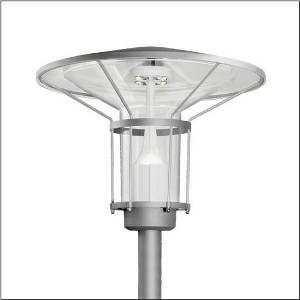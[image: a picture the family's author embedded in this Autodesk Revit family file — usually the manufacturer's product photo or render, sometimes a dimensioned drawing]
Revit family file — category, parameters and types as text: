
# Revit family: laterne_classic___st1_2a_5xa5245ef14h_27d9
name_source: partatom
category: Lighting Fixtures
units: mm (PartAtom-declared; Revit-internal decimal feet)

## family parameters
Cut with Voids When Loaded = No
Host = Face
Light Source = No
Part Type = Normal
Room Calculation Point = No
Round Connector Dimension = Use Diameter
Shared = No

## types (1)
- --- (1 x LED, 1380 lm, 10.5 W, 3000K)
    Apparent Load = 11 VA
    CIE Flux Codes = 21 60 93 97 100
    Color Rendering = 70
    Color Temperature = 3000K
    Default Elevation = 1800 mm
    Description = Lantern Classic, mast luminaire, Module 540 iQ-SR, primary light control with 3 zone facetted reflector, of plastic, silver coated, highly specular, structured, primary optical cover: cover, of PMMA, transparent, light distribution: ST1.2a, light emission: direct distribution, primary light characteristic: asymmetric, installation type: post-top, LED, High Power LED, rated luminous flux: 1.380lm, luminous efficacy: 131lm/W, light colour: 730, colour temperature: 3000K, control gear: ECG iQ, control: Auto-Match, Temp-Guard, Lumen-Switch, Night-Set, Smart-Wire, Light-Fading, Desk-Remote (wireless, voltage-free reading and setting of iQ features in the workshop via application-optimized NFC function/RFID function), optimised constant luminous flux control (CLO 2.0), Street-Remote, presetting dimming logarithmic, with terminal, 6-pole, max. 2.5mm², mains connection: 220..240V, AC, 50/60Hz, start of lifetime: 11W, end of lifetime: 11W, reduction: 5W, luminaire housing, upper part, of glass-fibre reinforced polyester, coated, Siteco® metallic grey (DB 702S), diameter: 750mm, height: 596mm, spigot size: d x l = 76 x 70mm (post-top) | with reducer (optional accessory) 60 x 70mm, post-top mast mounting element, of diecast aluminium, coated, Siteco® metallic grey (DB 702S), Module 540 iQ-SR, traffic white (RAL 9016), equipment: standard, protection rating (complete): IP65, insulation class (complete): insulation class II (safety insulation), certification: CE, ENEC, VDE, packaging unit: 1 piece

Light Distribution: ST1.2a
    Height = 596 mm
    Lamp = 1 x LED
    Lamp Light Flux = 1380 lm
    Lamp Power = 10.5 W
    Lamp count = 1
    Length = 750 mm
    Luminous efficacy = 131 lm/W
    Manufacturer = Siteco
    ModVariant = No
    Model = 5XA5245EF14H
    Number of Poles = 1
    OnlyDefault = Yes
    Power Factor = 1
    Product Name = Laterne Classic | ST1.2a
    Product group = mast luminaire | pylon top
    ProductGroupID = 6100
    Protection Class = Protection class II
    Protection Degree = IP 65
    RLX_Detail_Level = 1
    RlxData = <blob elided: 91801 chars, md5=6b808954>
    Socket = socket
    Standby Power = 0 W
    System Light Flux = 1380 lm
    System Power = 11 W
    Type Comments = factory setting: luminous flux: 100 % | dim-lin: 254 | 419 mA
    Type Image = l_1006052.jpg
    URL = http://relux.com
    VarID = @adj_071621
    Voltage = 0 V
    Weight = 0.00 kg
    Width = 0 mm  [stored 0 ft]

note: [stored X ft] marks values corroborated as IEEE doubles in the binary element streams (Revit-internal decimal feet)

## geometry (parser evidence)
native form markers: Blend x4, Sweep x11
no freeform markers — native parametric forms only
